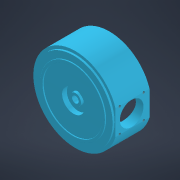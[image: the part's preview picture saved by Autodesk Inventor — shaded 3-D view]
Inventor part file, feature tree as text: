
AUTODESK INVENTOR PART (.ipt)
format: ipt  version: 2022 (Build 260153000, 153)  size: 226,304 bytes
history: native  units: mm
features: sketch x5, extrude x3, revolve x1, plane x1, chamfer x1, hole x1, pattern_circular x1, projected_geometry x1
ambient origin geometry x8: Origin, YZ Plane, XZ Plane, XY Plane, X Axis, Y Axis, Z Axis, Center Point
bodies: Solid1 (feature_tree)
feature tree (14):
  revolve  "Revolution1"  [1 undecoded]
  plane  "Work Plane1"
  extrude  "Extrusion5"  Depth=1.0mm
  chamfer  "Chamfer1"  Distance=30.0mm
  extrude  "Extrusion6"  Depth=10.0mm
  hole  "Hole2"  [1 undecoded]
  pattern_circular  "Circular Pattern1"  [2 undecoded]
  extrude  "Extrusion9"  Depth=2.0mm
  sketch  "Sketch1"  dims[d1=5.5mm d4=360.0deg d5=69.0mm]
  sketch  "Sketch7"  dims[d6=3.0mm d7=1.0mm]
  projected_geometry  "Projected Loop5"
  sketch  "Sketch8"  dims[d8=88.9mm]
  sketch  "Sketch10"  dims[d10=3.0mm]
  sketch  "Sketch12"  dims[d11=5.0mm d12=30.0mm d37=10.0mm d38=0.25mm d39=2.0mm d40=45.0deg d42=4.0mm d43=0.0mm d44=25.0mm d45=20.0mm d46=0.0mm d51=18.0mm d52=2.459mm d53=4.0mm d54=5.0mm d55=15.0mm d56=90.0deg d57=4.5mm d58=20.594885mm d59=40.0mm d60=360.0deg d64=38.0mm d65=45.0deg d74=7.0mm d75=24.0mm d76=3.0mm d77=2.5mm d78=3.0mm d79=115.0mm d80=60.150088mm d81=82.9mm d82=88.9mm d83=2.0mm d84=0.0mm]
note: 4 required parameter values undecoded (feature->parameter linkage not recoverable at this tier; creation-order binding heuristic only, values carry confidence <= 0.55)